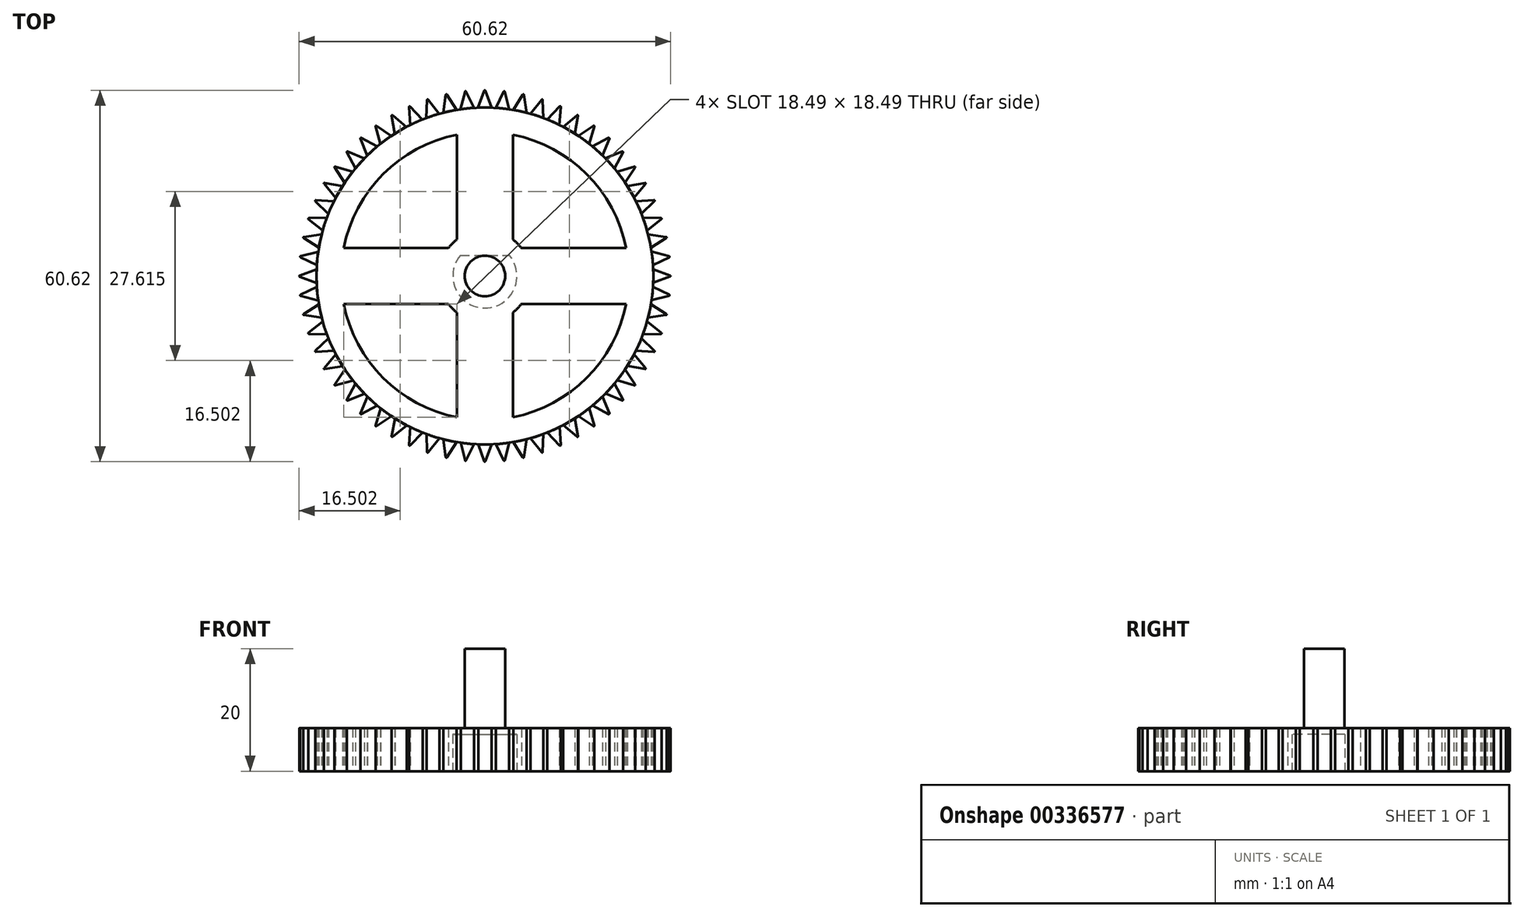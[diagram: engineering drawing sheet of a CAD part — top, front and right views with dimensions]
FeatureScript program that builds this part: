
annotation { "Feature Type Name" : "Feature", "Feature Type Description" : "" }
export const myFeature = defineFeature(function(context is Context, id is Id, definition is map)
    precondition{}
    {
        {
            var Q0;
            Q0=qCreatedBy(makeId("Top.planeOp"),FACE);
            var sketch = newSketch(context, id + "F0", { "sketchPlane" : qUnion([Q0])});
            skCircle(sketch, "E0", {"center": v(0, 0) * mm, "radius": 5.22 * mm});
            skCircle(sketch, "E1", {"center": v(0, 0) * mm, "radius": 27.5 * mm});
            skCircle(sketch, "E2", {"center": v(0, 0) * mm, "radius": 30.5 * mm});
            skLineSegment(sketch, "E3", {"start": v(-4, 3.36) * mm, "end": v(4, 3.36) * mm});
            skLineSegment(sketch, "E4", {"start": v(-0.1, 30.24) * mm, "end": v(-1.11, 27.48) * mm});
            skLineSegment(sketch, "E5", {"start": v(0.1, 30.24) * mm, "end": v(1.09, 27.48) * mm});
            skPoint(sketch, "E6.visualSharp", {"position": v(0, 30.5) * mm});
            skArc(sketch, "E6.filletArc", {"start": v(0.1, 30.24) * mm, "mid": v(0, 30.3) * mm, "end": v(-0.1, 30.24) * mm});
            skCircle(sketch, "E7", {"center": v(0, 0) * mm, "radius": 7.5 * mm});
            skCircle(sketch, "E8", {"center": v(0, 0) * mm, "radius": 23.5 * mm});
            skLineSegment(sketch, "E9", {"start": v(-4.56, 23.05) * mm, "end": v(-4.56, 5.95) * mm});
            skLineSegment(sketch, "E10", {"start": v(4.56, 23.05) * mm, "end": v(4.56, 5.95) * mm});
            skLineSegment(sketch, "E11", {"start": v(5.95, 4.56) * mm, "end": v(23.05, 4.56) * mm});
            skLineSegment(sketch, "E12", {"start": v(5.95, -4.56) * mm, "end": v(23.05, -4.56) * mm});
            skLineSegment(sketch, "E13", {"start": v(-5.95, 4.56) * mm, "end": v(-23.05, 4.56) * mm});
            skLineSegment(sketch, "E14", {"start": v(-5.95, -4.56) * mm, "end": v(-23.05, -4.56) * mm});
            skLineSegment(sketch, "E15", {"start": v(-4.56, -5.95) * mm, "end": v(-4.56, -23.05) * mm});
            skLineSegment(sketch, "E16", {"start": v(4.56, -5.95) * mm, "end": v(4.56, -23.05) * mm});
            skSolve(sketch);
        }
        {
            var Q0;
            {var subQ0=sQuery(id+"F0.wireOp",EDGE,"E4");Q0=makeQuery(id+"F0.imprint","IMPRINT",FACE,{"disambiguationData":[TD([[makeQuery(id+"F0.imprint","IMPRINT",EDGE,{"derivedFrom":subQ0}),1.0]])]});}
            extrude(context, id + "F1", {"entities" : qUnion([Q0]), "depth" : 7 * mm});
        }
        {
            var Q0;
            Q0=qCreatedBy(makeId("Right.planeOp"),FACE);
            var sketch = newSketch(context, id + "F2", { "sketchPlane" : qUnion([Q0])});
            skLineSegment(sketch, "E17", {"start": v(0, 0) * mm, "end": v(0, 28.66) * mm});
            skSolve(sketch);
        }
        {
            var Q0;
            Q0=makeQuery(id+"F1.opExtrude","SWEPT_BODY",BODY,{"disambiguationData":[OSD([sQuery(id+"F0.wireOp",EDGE,"E1"),sQuery(id+"F0.wireOp",EDGE,"E4"),sQuery(id+"F0.wireOp",EDGE,"E5"),sQuery(id+"F0.wireOp",EDGE,"E6.filletArc")])]});
            var Q1;
            Q1=sQuery(id+"F2.wireOp",EDGE,"E17");
            circularPattern(context, id + "F3", {"entities" : qUnion([Q0]), "axis" : qUnion([Q1]), "angle" : 360 * degree, "instanceCount" : 60, "equalSpace" : true});
        }
        {
            var Q0;
            {var subQ3=sQuery(id+"F0.wireOp",EDGE,"E1");var subQ4=makeQuery(id+"F0.imprint","INTERSECT",VERTEX,{"derivedFrom":[subQ3,sQuery(id+"F0.wireOp",EDGE,"E4")]});Q0=makeQuery(id+"F0.imprint","IMPRINT",FACE,{"disambiguationData":[TD([[makeQuery(id+"F0.imprint","IMPRINT",EDGE,{"disambiguationData":[TD([[subQ4,1.0]])],"derivedFrom":subQ3}),1.0]])]});}
            var Q1;
            {var subQ0=sQuery(id+"F0.wireOp",EDGE,"E9");Q1=makeQuery(id+"F0.imprint","IMPRINT",FACE,{"disambiguationData":[TD([[makeQuery(id+"F0.imprint","IMPRINT",EDGE,{"derivedFrom":subQ0}),1.0]])]});}
            var Q2;
            {var subQ0=sQuery(id+"F0.wireOp",EDGE,"E13");Q2=makeQuery(id+"F0.imprint","IMPRINT",FACE,{"disambiguationData":[TD([[makeQuery(id+"F0.imprint","IMPRINT",EDGE,{"derivedFrom":subQ0}),1.0]])]});}
            var Q3;
            {var subQ0=sQuery(id+"F0.wireOp",EDGE,"E15");Q3=makeQuery(id+"F0.imprint","IMPRINT",FACE,{"disambiguationData":[TD([[makeQuery(id+"F0.imprint","IMPRINT",EDGE,{"derivedFrom":subQ0}),1.0]])]});}
            var Q4;
            {var subQ0=sQuery(id+"F0.wireOp",EDGE,"E11");Q4=makeQuery(id+"F0.imprint","IMPRINT",FACE,{"disambiguationData":[TD([[makeQuery(id+"F0.imprint","IMPRINT",EDGE,{"derivedFrom":subQ0}),-1.0]])]});}
            var Q5;
            {var subQ3=sQuery(id+"F0.wireOp",EDGE,"E3");var subQ4=sQuery(id+"F0.wireOp",EDGE,"E0");var subQ5=makeQuery(id+"F0.imprint","INTERSECT",VERTEX,{"disambiguationData":[OD(0.0)],"derivedFrom":[subQ4,subQ3]});Q5=makeQuery(id+"F0.imprint","IMPRINT",FACE,{"disambiguationData":[TD([[makeQuery(id+"F0.imprint","IMPRINT",EDGE,{"disambiguationData":[TD([[subQ5,1.0]])],"derivedFrom":subQ4}),-1.0]])]});}
            var Q6;
            {var subQ0=sQuery(id+"F0.wireOp",EDGE,"E3");Q6=makeQuery(id+"F0.imprint","IMPRINT",FACE,{"disambiguationData":[TD([[makeQuery(id+"F0.imprint","IMPRINT",EDGE,{"derivedFrom":subQ0}),1.0]])]});}
            extrude(context, id + "F4", {"entities" : qUnion([Q0, Q1, Q2, Q3, Q4, Q5, Q6]), "depth" : 7 * mm});
        }
        {
            var Q0;
            Q0=makeQuery(id+"F4.opExtrude","CAP_FACE",FACE,{"disambiguationData":[OSD([sQuery(id+"F0.wireOp",EDGE,"E0"),sQuery(id+"F0.wireOp",EDGE,"E1"),sQuery(id+"F0.wireOp",EDGE,"E3"),sQuery(id+"F0.wireOp",EDGE,"E7"),sQuery(id+"F0.wireOp",EDGE,"E8"),sQuery(id+"F0.wireOp",EDGE,"E9"),sQuery(id+"F0.wireOp",EDGE,"E10"),sQuery(id+"F0.wireOp",EDGE,"E11"),sQuery(id+"F0.wireOp",EDGE,"E12"),sQuery(id+"F0.wireOp",EDGE,"E13"),sQuery(id+"F0.wireOp",EDGE,"E14"),sQuery(id+"F0.wireOp",EDGE,"E15"),sQuery(id+"F0.wireOp",EDGE,"E16")])],"isStart":false});
            var sketch = newSketch(context, id + "F5", { "sketchPlane" : qUnion([Q0])});
            skCircle(sketch, "E18", {"center": v(0, 0) * mm, "radius": 5.25 * mm});
            skLineSegment(sketch, "E19", {"start": v(-4, 3.36) * mm, "end": v(4, 3.36) * mm});
            skSolve(sketch);
        }
        {
            var Q0;
            {var subQ0=sQuery(id+"F5.wireOp",EDGE,"E19");Q0=makeQuery(id+"F5.imprint","IMPRINT",FACE,{"disambiguationData":[TD([[makeQuery(id+"F5.imprint","IMPRINT",EDGE,{"derivedFrom":subQ0}),-1.0]])]});}
            extrude(context, id + "F6", {"entities" : qUnion([Q0]), "operationType" : NewBodyOperationType.ADD, "depth" : -1 * mm});
        }
        {
            var Q0;
            Q0=makeQuery(id+"F6.boolean.opBoolean","MERGE",FACE,{"derivedFrom":[makeQuery(id+"F4.opExtrude","CAP_FACE",FACE,{"disambiguationData":[OSD([sQuery(id+"F0.wireOp",EDGE,"E0"),sQuery(id+"F0.wireOp",EDGE,"E1"),sQuery(id+"F0.wireOp",EDGE,"E3"),sQuery(id+"F0.wireOp",EDGE,"E7"),sQuery(id+"F0.wireOp",EDGE,"E8"),sQuery(id+"F0.wireOp",EDGE,"E9"),sQuery(id+"F0.wireOp",EDGE,"E10"),sQuery(id+"F0.wireOp",EDGE,"E11"),sQuery(id+"F0.wireOp",EDGE,"E12"),sQuery(id+"F0.wireOp",EDGE,"E13"),sQuery(id+"F0.wireOp",EDGE,"E14"),sQuery(id+"F0.wireOp",EDGE,"E15"),sQuery(id+"F0.wireOp",EDGE,"E16")])],"isStart":false}),makeQuery(id+"F6.opExtrude","CAP_FACE",FACE,{"disambiguationData":[OSD([sQuery(id+"F5.wireOp",EDGE,"E18"),sQuery(id+"F5.wireOp",EDGE,"E19")])],"isStart":true})]});
            var sketch = newSketch(context, id + "F7", { "sketchPlane" : qUnion([Q0])});
            skCircle(sketch, "E20", {"center": v(0, 0) * mm, "radius": 3.3 * mm});
            skSolve(sketch);
        }
        {
            var Q0;
            Q0=makeQuery(id+"F7.imprint","IMPRINT",FACE,{"disambiguationData":[TD([[makeQuery(id+"F7.imprint","IMPRINT",EDGE,{"derivedFrom":sQuery(id+"F7.wireOp",EDGE,"E20")}),1.0]])]});
            extrude(context, id + "F8", {"entities" : qUnion([Q0]), "operationType" : NewBodyOperationType.ADD, "depth" : 13 * mm});
        }
    });
